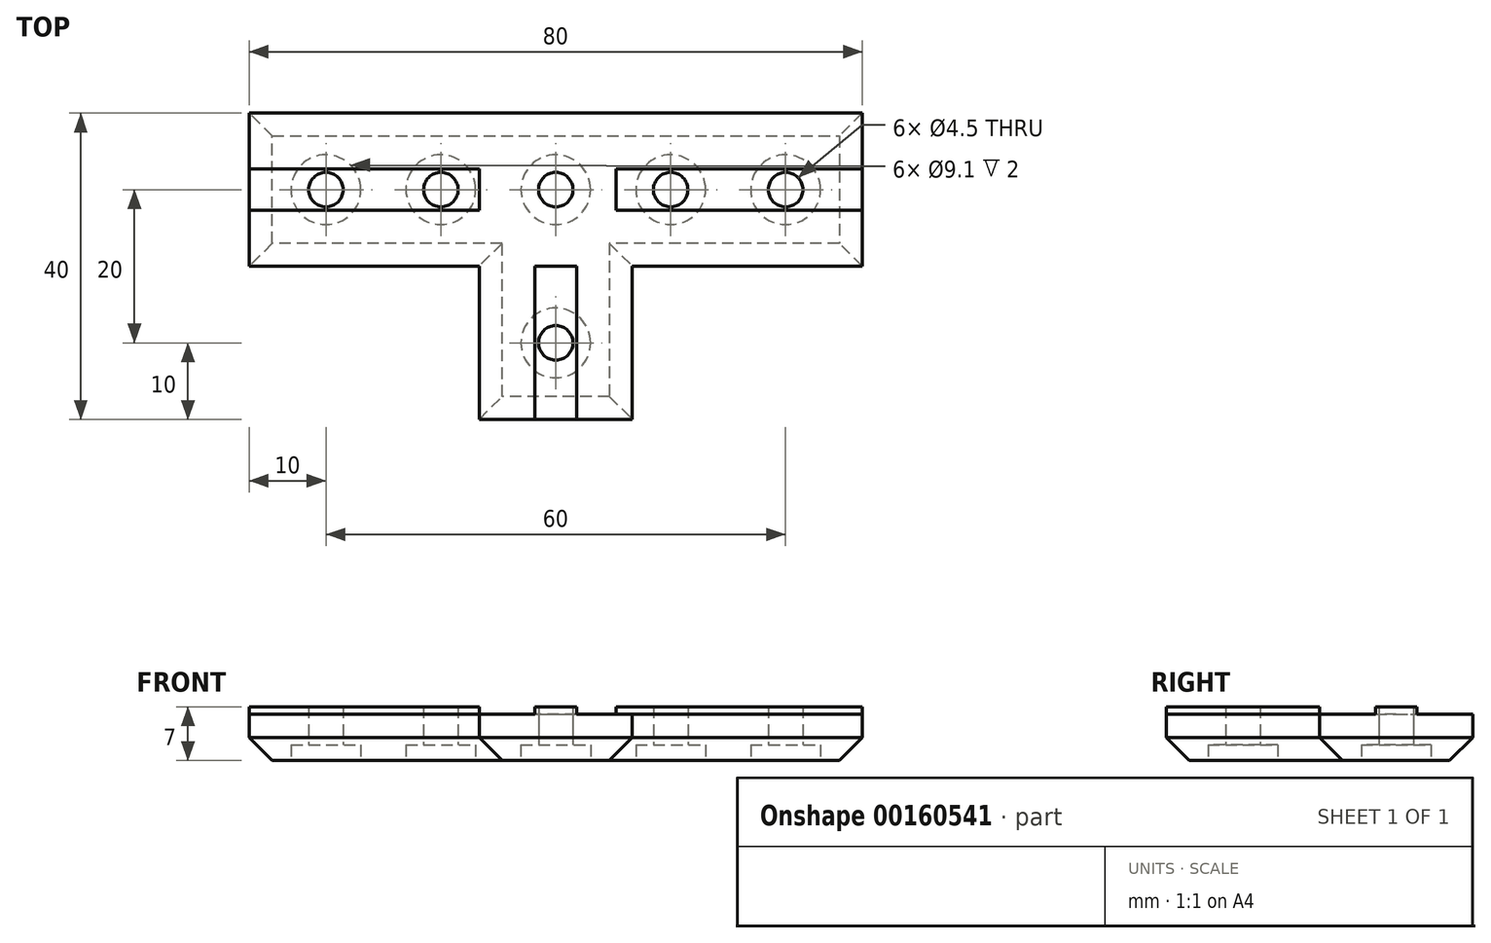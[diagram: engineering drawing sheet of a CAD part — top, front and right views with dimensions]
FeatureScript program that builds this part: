
annotation { "Feature Type Name" : "Feature", "Feature Type Description" : "" }
export const myFeature = defineFeature(function(context is Context, id is Id, definition is map)
    precondition{}
    {
        {
            var Q0;
            Q0=qCreatedBy(makeId("Top.planeOp"),FACE);
            var sketch = newSketch(context, id + "F0", { "sketchPlane" : qUnion([Q0])});
            skLineSegment(sketch, "E0", {"start": v(0, 0) * mm, "end": v(0, 20) * mm, "construction": true});
            skLineSegment(sketch, "E1", {"start": v(0, 0) * mm, "end": v(0, -20) * mm, "construction": true});
            skLineSegment(sketch, "E2", {"start": v(-10, 0) * mm, "end": v(-40, 0) * mm});
            skLineSegment(sketch, "E3", {"start": v(0, 20) * mm, "end": v(-40, 20) * mm});
            skLineSegment(sketch, "E4", {"start": v(-40, 20) * mm, "end": v(-40, 0) * mm});
            skLineSegment(sketch, "E5", {"start": v(0, 20) * mm, "end": v(40, 20) * mm});
            skLineSegment(sketch, "E6", {"start": v(40, 20) * mm, "end": v(40, 0) * mm});
            skLineSegment(sketch, "E7", {"start": v(40, 0) * mm, "end": v(10, 0) * mm});
            skLineSegment(sketch, "E8", {"start": v(0, -20) * mm, "end": v(10, -20) * mm});
            skLineSegment(sketch, "E9", {"start": v(10, -20) * mm, "end": v(10, 0) * mm});
            skLineSegment(sketch, "E10", {"start": v(0, -20) * mm, "end": v(-10, -20) * mm});
            skLineSegment(sketch, "E11", {"start": v(-10, -20) * mm, "end": v(-10, 0) * mm});
            skSolve(sketch);
        }
        {
            var Q0;
            Q0=qSketchRegion(id+"F0",true);
            extrude(context, id + "F1", {"entities" : qUnion([Q0]), "depth" : 6 * mm});
        }
        {
            var Q0;
            Q0=makeQuery(id+"F1.opExtrude","CAP_FACE",FACE,{"disambiguationData":[OSD([sQuery(id+"F0.wireOp",EDGE,"E2"),sQuery(id+"F0.wireOp",EDGE,"E3"),sQuery(id+"F0.wireOp",EDGE,"E4"),sQuery(id+"F0.wireOp",EDGE,"E5"),sQuery(id+"F0.wireOp",EDGE,"E6"),sQuery(id+"F0.wireOp",EDGE,"E7"),sQuery(id+"F0.wireOp",EDGE,"E8"),sQuery(id+"F0.wireOp",EDGE,"E9"),sQuery(id+"F0.wireOp",EDGE,"E10"),sQuery(id+"F0.wireOp",EDGE,"E11")])],"isStart":false});
            var sketch = newSketch(context, id + "F2", { "sketchPlane" : qUnion([Q0])});
            skLineSegment(sketch, "E12", {"start": v(-40, 10) * mm, "end": v(40, 10) * mm, "construction": true});
            skLineSegment(sketch, "E13", {"start": v(0, -20) * mm, "end": v(0, 0) * mm, "construction": true});
            skLineSegment(sketch, "E14", {"start": v(0, 0) * mm, "end": v(-2.71, 0) * mm});
            skLineSegment(sketch, "E15", {"start": v(-2.71, 0) * mm, "end": v(-2.7, -20) * mm});
            skLineSegment(sketch, "E16", {"start": v(2.71, -20) * mm, "end": v(2.71, 0) * mm});
            skLineSegment(sketch, "E17", {"start": v(2.71, 0) * mm, "end": v(0, 0) * mm});
            skLineSegment(sketch, "E18", {"start": v(-2.7, -20) * mm, "end": v(2.71, -20) * mm});
            skLineSegment(sketch, "E19", {"start": v(7.85, 10) * mm, "end": v(7.85, 12.71) * mm});
            skLineSegment(sketch, "E20", {"start": v(7.85, 12.71) * mm, "end": v(40, 12.71) * mm});
            skLineSegment(sketch, "E21", {"start": v(40, 12.7) * mm, "end": v(40, 7.3) * mm});
            skLineSegment(sketch, "E22", {"start": v(40, 7.3) * mm, "end": v(7.85, 7.29) * mm});
            skLineSegment(sketch, "E23", {"start": v(7.85, 7.29) * mm, "end": v(7.85, 10) * mm});
            skLineSegment(sketch, "E24", {"start": v(-40, 12.7) * mm, "end": v(-40, 7.29) * mm});
            skLineSegment(sketch, "E25", {"start": v(-40, 7.29) * mm, "end": v(-10, 7.29) * mm});
            skLineSegment(sketch, "E26", {"start": v(-10, 7.29) * mm, "end": v(-10, 12.71) * mm});
            skLineSegment(sketch, "E27", {"start": v(-10, 12.71) * mm, "end": v(-40, 12.71) * mm});
            skSolve(sketch);
        }
        {
            var Q0;
            Q0=qSketchRegion(id+"F2",true);
            extrude(context, id + "F3", {"entities" : qUnion([Q0]), "operationType" : NewBodyOperationType.ADD, "flatOperationType" : FlatOperationType.REMOVE, "offsetDistance" : 25 * mm, "depth" : 1 * mm, "domain" : OperationDomain.MODEL});
        }
        {
            var Q0;
            Q0=makeQuery(id+"F1.opExtrude","CAP_FACE",FACE,{"disambiguationData":[OSD([sQuery(id+"F0.wireOp",EDGE,"E2"),sQuery(id+"F0.wireOp",EDGE,"E3"),sQuery(id+"F0.wireOp",EDGE,"E4"),sQuery(id+"F0.wireOp",EDGE,"E5"),sQuery(id+"F0.wireOp",EDGE,"E6"),sQuery(id+"F0.wireOp",EDGE,"E7"),sQuery(id+"F0.wireOp",EDGE,"E8"),sQuery(id+"F0.wireOp",EDGE,"E9"),sQuery(id+"F0.wireOp",EDGE,"E10"),sQuery(id+"F0.wireOp",EDGE,"E11")])],"isStart":true});
            var sketch = newSketch(context, id + "F4", { "sketchPlane" : qUnion([Q0])});
            skCircle(sketch, "E28", {"center": v(-30, -10) * mm, "radius": 2.25 * mm});
            skCircle(sketch, "E29", {"center": v(0, -10) * mm, "radius": 2.25 * mm});
            skCircle(sketch, "E30", {"center": v(0, 10) * mm, "radius": 2.25 * mm});
            skCircle(sketch, "E31", {"center": v(30, -10) * mm, "radius": 2.25 * mm});
            skCircle(sketch, "E32", {"center": v(15, -10) * mm, "radius": 2.25 * mm});
            skCircle(sketch, "E33", {"center": v(-15, -10) * mm, "radius": 2.25 * mm});
            skSolve(sketch);
        }
        {
            var Q0;
            Q0=qSketchRegion(id+"F4",true);
            extrude(context, id + "F5", {"entities" : qUnion([Q0]), "operationType" : NewBodyOperationType.REMOVE, "endBound" : BoundingType.THROUGH_ALL, "oppositeDirection" : true, "depth" : 25 * mm});
        }
        {
            var Q0;
            Q0=makeQuery(id+"F1.opExtrude","CAP_FACE",FACE,{"disambiguationData":[OSD([sQuery(id+"F0.wireOp",EDGE,"E2"),sQuery(id+"F0.wireOp",EDGE,"E3"),sQuery(id+"F0.wireOp",EDGE,"E4"),sQuery(id+"F0.wireOp",EDGE,"E5"),sQuery(id+"F0.wireOp",EDGE,"E6"),sQuery(id+"F0.wireOp",EDGE,"E7"),sQuery(id+"F0.wireOp",EDGE,"E8"),sQuery(id+"F0.wireOp",EDGE,"E9"),sQuery(id+"F0.wireOp",EDGE,"E10"),sQuery(id+"F0.wireOp",EDGE,"E11")])],"isStart":true});
            var sketch = newSketch(context, id + "F6", { "sketchPlane" : qUnion([Q0])});
            skCircle(sketch, "E34", {"center": v(0, 10) * mm, "radius": 4.55 * mm});
            skCircle(sketch, "E35", {"center": v(0, -10) * mm, "radius": 4.55 * mm});
            skCircle(sketch, "E36", {"center": v(30, -10) * mm, "radius": 4.55 * mm});
            skCircle(sketch, "E37", {"center": v(-30, -10) * mm, "radius": 4.55 * mm});
            skCircle(sketch, "E38", {"center": v(-15, -10) * mm, "radius": 4.55 * mm});
            skCircle(sketch, "E39", {"center": v(15, -10) * mm, "radius": 4.55 * mm});
            skSolve(sketch);
        }
        {
            var Q0;
            Q0=qSketchRegion(id+"F6",true);
            extrude(context, id + "F7", {"entities" : qUnion([Q0]), "operationType" : NewBodyOperationType.REMOVE, "oppositeDirection" : true, "depth" : 2 * mm});
        }
        {
            var Q0;
            Q0=makeQuery(id+"F1.opExtrude","CAP_EDGE",EDGE,{"disambiguationData":[OSD([sQuery(id+"F0.wireOp",EDGE,"E11")])],"isStart":true});
            var Q1;
            Q1=makeQuery(id+"F1.opExtrude","CAP_EDGE",EDGE,{"disambiguationData":[OSD([sQuery(id+"F0.wireOp",EDGE,"E2")])],"isStart":true});
            var Q2;
            Q2=makeQuery(id+"F1.opExtrude","CAP_EDGE",EDGE,{"disambiguationData":[OSD([sQuery(id+"F0.wireOp",EDGE,"E9")])],"isStart":true});
            var Q3;
            Q3=makeQuery(id+"F1.opExtrude","CAP_EDGE",EDGE,{"disambiguationData":[OSD([sQuery(id+"F0.wireOp",EDGE,"E7")])],"isStart":true});
            var Q4;
            Q4=makeQuery(id+"F1.opExtrude","CAP_EDGE",EDGE,{"disambiguationData":[OSD([sQuery(id+"F0.wireOp",EDGE,"E3"),sQuery(id+"F0.wireOp",EDGE,"E5")])],"isStart":true});
            var Q5;
            Q5=makeQuery(id+"F1.opExtrude","CAP_EDGE",EDGE,{"disambiguationData":[OSD([sQuery(id+"F0.wireOp",EDGE,"E6")])],"isStart":true});
            var Q6;
            Q6=makeQuery(id+"F1.opExtrude","CAP_EDGE",EDGE,{"disambiguationData":[OSD([sQuery(id+"F0.wireOp",EDGE,"E4")])],"isStart":true});
            var Q7;
            Q7=makeQuery(id+"F1.opExtrude","CAP_EDGE",EDGE,{"disambiguationData":[OSD([sQuery(id+"F0.wireOp",EDGE,"E8"),sQuery(id+"F0.wireOp",EDGE,"E10")])],"isStart":true});
            chamfer(context, id + "F8", {"entities" : qUnion([Q0, Q1, Q2, Q3, Q4, Q5, Q6, Q7]), "width" : 3 * mm, "tangentPropagation" : true});
        }
    });
